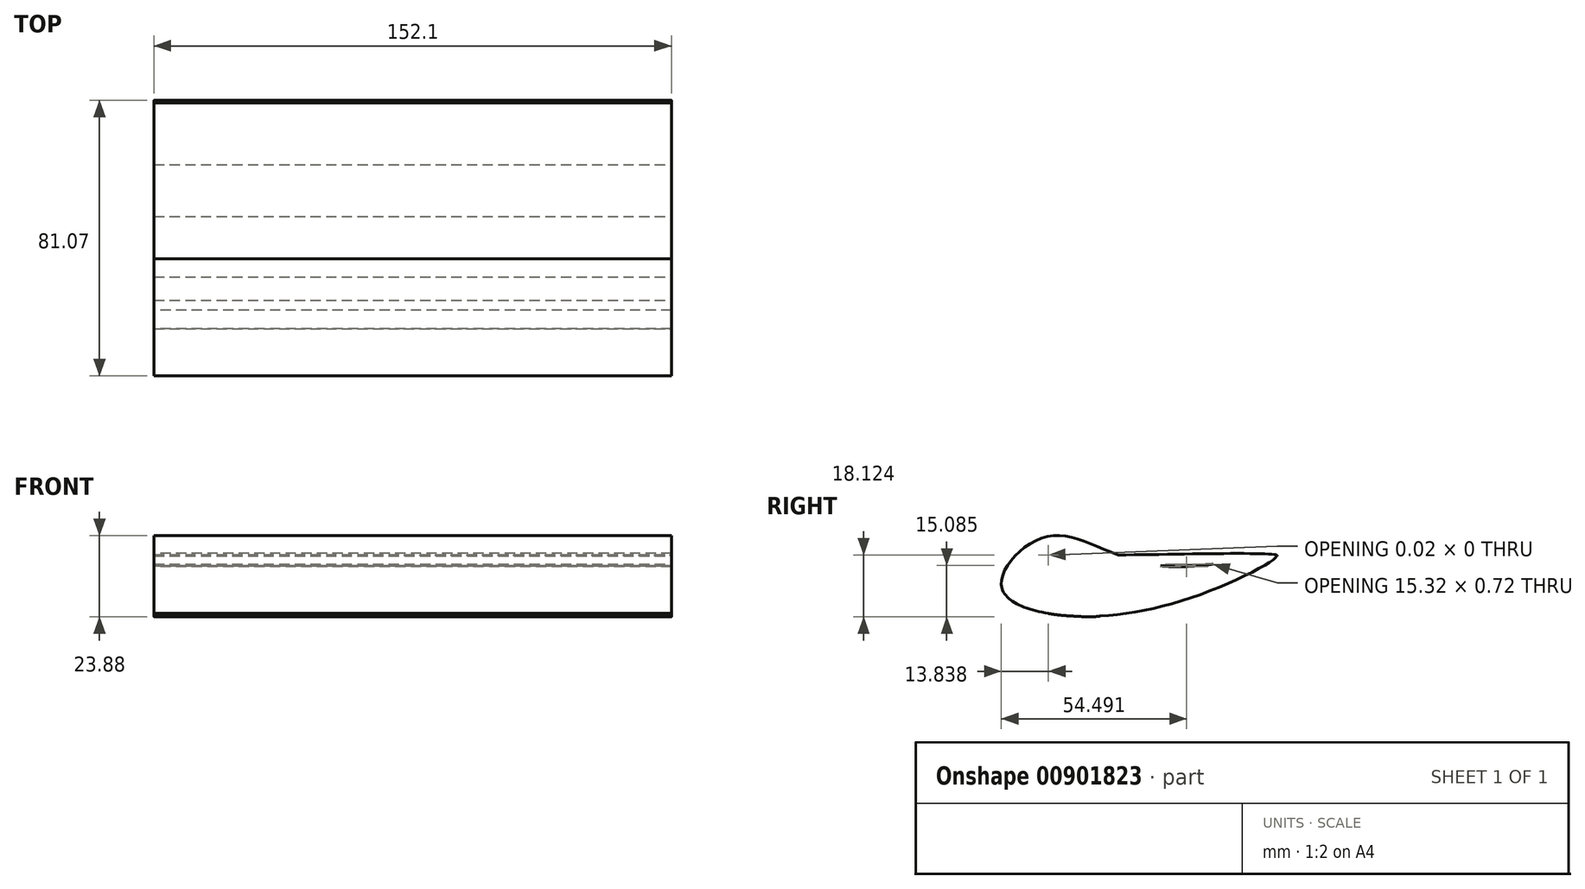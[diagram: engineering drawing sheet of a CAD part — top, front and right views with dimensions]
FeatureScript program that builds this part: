
annotation { "Feature Type Name" : "Feature", "Feature Type Description" : "" }
export const myFeature = defineFeature(function(context is Context, id is Id, definition is map)
    precondition{}
    {
        {
            var Q0;
            Q0=qCreatedBy(makeId("Front.planeOp"),FACE);
            var sketch = newSketch(context, id + "F0", { "sketchPlane" : qUnion([Q0])});
            skLineSegment(sketch, "E0.bottom", {"start": v(76.05, 8.57) * mm, "end": v(-76.05, 8.57) * mm});
            skLineSegment(sketch, "E0.top", {"start": v(76.05, -8.57) * mm, "end": v(-76.05, -8.57) * mm});
            skLineSegment(sketch, "E0.left", {"start": v(76.05, 8.57) * mm, "end": v(76.05, -8.57) * mm});
            skLineSegment(sketch, "E0.right", {"start": v(-76.05, 8.57) * mm, "end": v(-76.05, -8.57) * mm});
            skPoint(sketch, "E0.middle", {"position": v(0, 0) * mm});
            skSolve(sketch);
        }
        {
            var Q0;
            Q0 = qSketchRegion(id + "F0", true);
            extrude(context, id + "F1", {"entities" : qUnion([Q0]), "depth" : 0.03 * mm, "offsetDistance" : 25.4 * mm});
        }
        {
            var Q0;
            Q0=makeQuery(id+"F1.opExtrude","SWEPT_FACE",FACE,{"disambiguationData":[OSD([sQuery(id+"F0.wireOp",EDGE,"E0.left")])]});
            var sketch = newSketch(context, id + "F2", { "sketchPlane" : qUnion([Q0])});
            skLineSegment(sketch, "E1", {"start": v(-0.03, 8.57) * mm, "end": v(0, 8.57) * mm});
            skFitSpline(sketch, "E2", {"points": [v(0, 8.57) * mm, v(32.98, 5.43) * mm, v(67.09, 8.57) * mm, v(10.86, 8.57) * mm, v(0, 8.57) * mm]});
            skFitSpline(sketch, "E3", {"points": [v(0, -8.57) * mm, v(42.94, -3.6) * mm, v(67.09, 8.57) * mm, v(32.98, 5.43) * mm, v(0, 14.1) * mm, v(-13.84, 0) * mm, v(0, -8.57) * mm]});
            skLineSegment(sketch, "E4", {"start": v(0, 0) * mm, "end": v(-13.84, 0) * mm});
            skFitSpline(sketch, "E5", {"points": [v(0, 8.57) * mm, v(-0.03, 8.57) * mm, v(-7.3, 8.57) * mm, v(-11.47, 4.98) * mm, v(-11.21, -3.36) * mm, v(0, -8.57) * mm, v(8.36, -9.4) * mm, v(17.34, -7.4) * mm, v(0, 8.57) * mm]});
            skSolve(sketch);
        }
        {
            var Q0;
            Q0 = qSketchRegion(id + "F2", true);
            extrude(context, id + "F3", {"entities" : qUnion([Q0]), "operationType" : NewBodyOperationType.ADD, "oppositeDirection" : true, "depth" : 78.74 * mm, "offsetDistance" : 25.4 * mm});
        }
        {
            var Q0;
            Q0=makeQuery(id+"F1.opExtrude","SWEPT_BODY",BODY,{"disambiguationData":[OSD([sQuery(id+"F0.wireOp",EDGE,"E0.bottom"),sQuery(id+"F0.wireOp",EDGE,"E0.top"),sQuery(id+"F0.wireOp",EDGE,"E0.left"),sQuery(id+"F0.wireOp",EDGE,"E0.right")])]});
            var Q1;
            Q1=qCreatedBy(makeId("Right.planeOp"),FACE);
            mirror(context, id + "F4", {"operationType" : NewBodyOperationType.ADD, "entities" : qUnion([Q0]), "mirrorPlane" : qUnion([Q1])});
        }
    });
